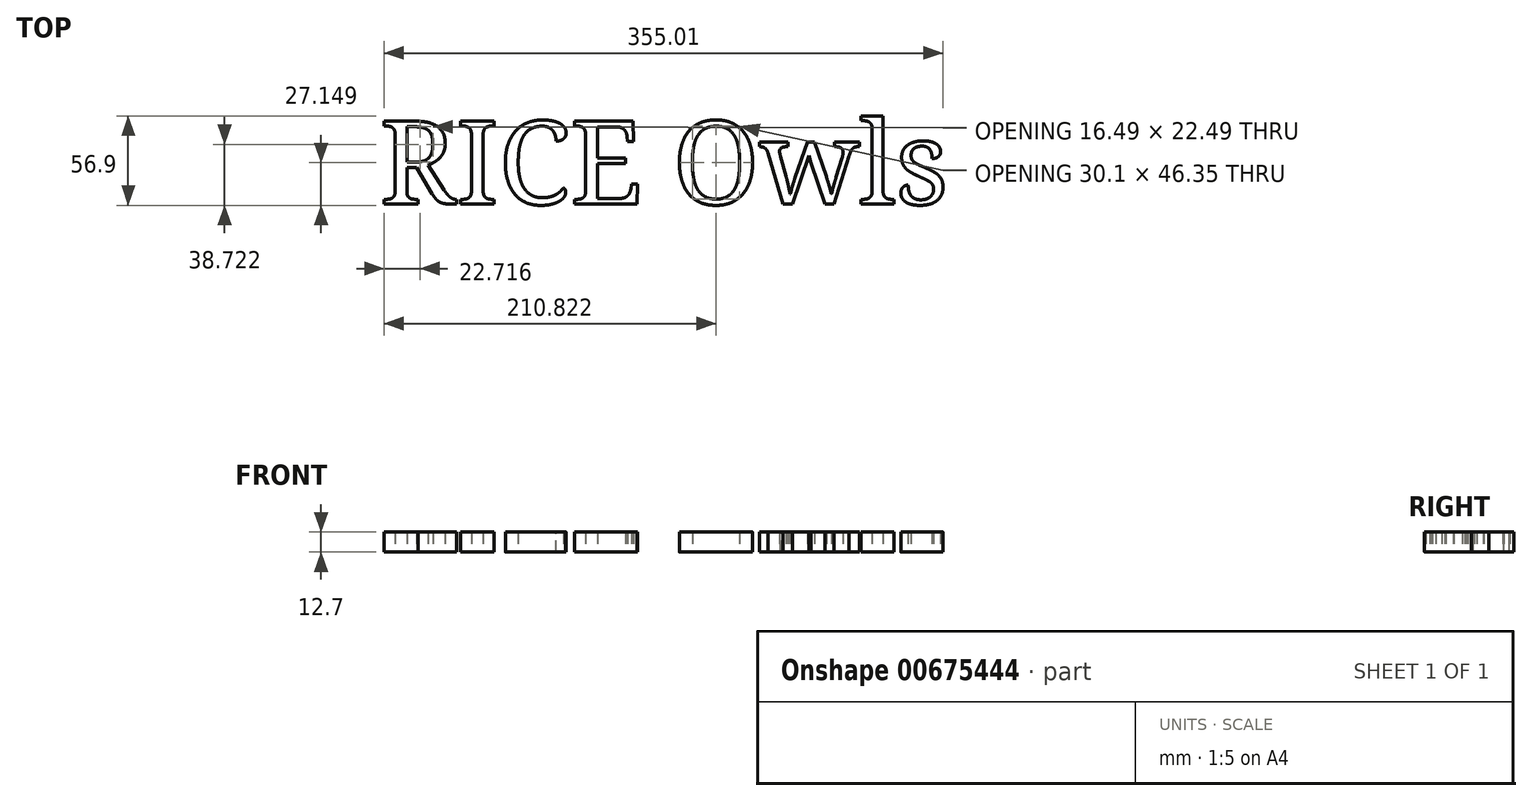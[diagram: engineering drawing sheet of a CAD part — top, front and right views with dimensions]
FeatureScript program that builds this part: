
annotation { "Feature Type Name" : "Feature", "Feature Type Description" : "" }
export const myFeature = defineFeature(function(context is Context, id is Id, definition is map)
    precondition{}
    {
        {
            var Q0;
            Q0=qCreatedBy(makeId("Top.planeOp"),FACE);
            var sketch = newSketch(context, id + "F0", { "sketchPlane" : qUnion([Q0])});
            skText(sketch, "E0", { "text": "RICE Owls\n", "fontName": "NotoSerif-Regular.ttf"});
            const initialGuessF0  = {"E0": [-0.14563, -0.02652, 1, 0, 0.05322]};
            skSetInitialGuess(sketch, initialGuessF0);
            skSolve(sketch);
        }
        {
            var Q0;
            Q0 = qSketchRegion(id + "F0", true);
            extrude(context, id + "F1", {"entities" : qUnion([Q0]), "depth" : 12.7 * mm, "offsetDistance" : 25.4 * mm});
        }
    });
